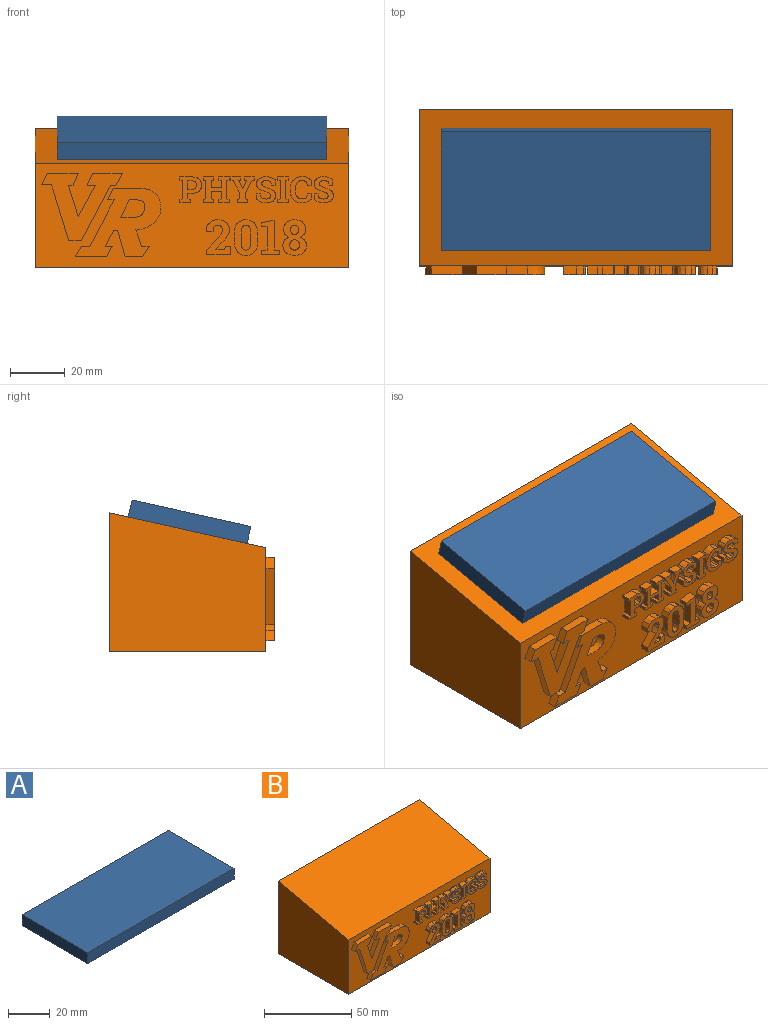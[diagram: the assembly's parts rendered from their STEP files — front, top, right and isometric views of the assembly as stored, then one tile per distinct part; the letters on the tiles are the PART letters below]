
ASSEMBLY  parts=2 mates=1
PART A: 6 faces, bbox 98.4x44.5x6.4 mm
  f0: plane 44.45x6.35mm, normal (-1,0,0), area 282.3mm2, adj f1,f3,f4,f5
  f1: plane 98.43x6.35mm, normal (0,-1,0), area 625mm2, adj f0,f2,f4,f5
  f2: plane 44.45x6.35mm, normal (1,0,0), area 282.3mm2, adj f1,f3,f4,f5
  f3: plane 98.43x6.35mm, normal (0,1,0), area 625mm2, adj f0,f2,f4,f5
  f4: plane 98.43x44.45mm, normal (0,0,1), area 4375mm2, adj f0,f1,f2,f3
  f5: plane 98.43x44.45mm, normal (0,0,-1), area 4375mm2, adj f0,f1,f2,f3
PART B: 311 faces, bbox 114.3x60.3x50.8 mm
  f0: plane 114.3x38.1mm, normal (0,-1,0), area 3082.9mm2, adj f1,f2,f4,f5,f12,f13,f14,f15
  f1: plane 57.15x50.8mm, normal (-1,0,0), area 2540.3mm2, adj f0,f3,f4,f5
  f2: plane 57.15x50.8mm, normal (1,0,0), area 2540.3mm2, adj f0,f3,f4,f5
  f3: plane 114.3x50.8mm, normal (0,1,0), area 5806.4mm2, adj f1,f2,f4,f5
  f4: plane 114.3x57.15mm, normal (0,0,-1), area 6532.2mm2, adj f0,f1,f2,f3
  f5: plane 114.3x57.15mm, normal (0,-0.22,0.98), area 6691.6mm2, adj f0,f1,f2,f3
  f6: plane 3.18x1.58mm, normal (0,0,1), area 5mm2, adj f7,f27,f28,f29
  f7: plane 3.18x3.07mm, normal (1,0,0), area 9.7mm2, adj f6,f8,f28,f29
  f8: plane 3.18x1.58mm, normal (0,0,-1), area 5mm2, adj f7,f9,f28,f29
  f9: extruded ~3.18x1.18mm, area 4.1mm2, adj f8,f10,f28,f29
  f10: extruded ~3.18x1.11mm, area 3.8mm2, adj f9,f11,f28,f29
  f11: extruded ~3.18x1.09mm, area 3.8mm2, adj f10,f27,f28,f29
  f12: extruded ~3.18x2.53mm, area 8.6mm2, adj f0,f13,f26,f28
  f13: plane 4.44x3.18mm, normal (0,0,1), area 14.1mm2, adj f0,f12,f14,f28
  f14: plane 3.18x1.13mm, normal (-1,0,0), area 3.6mm2, adj f0,f13,f15,f28
  f15: plane 3.18x0.99mm, normal (-0.19,0,-0.98), area 3.2mm2, adj f0,f14,f16,f28
  f16: plane 6.7x3.18mm, normal (-1,0,0), area 21.3mm2, adj f0,f15,f17,f28
  f17: plane 3.18x0.99mm, normal (-0.19,0,0.98), area 3.2mm2, adj f0,f16,f18,f28
  f18: plane 3.18x1.12mm, normal (-1,0,0), area 3.6mm2, adj f0,f17,f19,f28
  f19: plane 3.87x3.18mm, normal (0,0,-1), area 12.3mm2, adj f0,f18,f20,f28
  f20: plane 3.18x1.12mm, normal (1,0,0), area 3.6mm2, adj f0,f19,f21,f28
  f21: plane 3.18x1mm, normal (0.19,0,0.98), area 3.2mm2, adj f0,f20,f22,f28
  f22: plane 3.18x2.07mm, normal (1,0,0), area 6.6mm2, adj f0,f21,f23,f28
  f23: plane 3.18x1.58mm, normal (0,0,-1), area 5mm2, adj f0,f22,f24,f28
  f24: extruded ~3.18x2.53mm, area 8.6mm2, adj f0,f23,f25,f28
  f25: extruded ~3.18x2.15mm, area 7.7mm2, adj f0,f24,f26,f28
  f26: extruded ~3.18x2.16mm, area 7.7mm2, adj f0,f12,f25,f28
  f27: extruded ~3.18x1.18mm, area 4.1mm2, adj f6,f11,f28,f29
  f28: plane 9.33x7.9mm, normal (0,-1,0), area 38.4mm2, adj f6,f7,f8,f9,f10,f11,f12,f13
  f29: plane 3.16x3.07mm, normal (0,-1,0), area 8.8mm2, adj f6,f7,f8,f9,f10,f11,f27
  f30: plane 3.18x1.13mm, normal (-1,0,0), area 3.6mm2, adj f0,f31,f57,f58
  f31: plane 3.18x0.99mm, normal (-0.19,0,-0.98), area 3.2mm2, adj f0,f30,f32,f58
  f32: plane 6.7x3.18mm, normal (-1,0,0), area 21.3mm2, adj f0,f31,f33,f58
  f33: plane 3.18x0.99mm, normal (-0.19,0,0.98), area 3.2mm2, adj f0,f32,f34,f58
  f34: plane 3.18x1.12mm, normal (-1,0,0), area 3.6mm2, adj f0,f33,f35,f58
  f35: plane 3.87x3.18mm, normal (0,0,-1), area 12.3mm2, adj f0,f34,f36,f58
  f36: plane 3.18x1.12mm, normal (1,0,0), area 3.6mm2, adj f0,f35,f37,f58
  f37: plane 3.18x1mm, normal (0.19,0,0.98), area 3.2mm2, adj f0,f36,f38,f58
  f38: plane 3.18x2.56mm, normal (1,0,0), area 8.1mm2, adj f0,f37,f39,f58
  f39: plane 3.81x3.18mm, normal (0,0,-1), area 12.1mm2, adj f0,f38,f40,f58
  f40: plane 3.18x2.56mm, normal (-1,0,0), area 8.1mm2, adj f0,f39,f41,f58
  f41: plane 3.18x1mm, normal (-0.19,0,0.98), area 3.2mm2, adj f0,f40,f42,f58
  f42: plane 3.18x1.12mm, normal (-1,0,0), area 3.6mm2, adj f0,f41,f43,f58
  f43: plane 3.87x3.18mm, normal (0,0,-1), area 12.3mm2, adj f0,f42,f44,f58
  f44: plane 3.18x1.12mm, normal (1,0,0), area 3.6mm2, adj f0,f43,f45,f58
  f45: plane 3.18x1mm, normal (0.19,0,0.98), area 3.2mm2, adj f0,f44,f46,f58
  f46: plane 6.7x3.18mm, normal (1,0,0), area 21.3mm2, adj f0,f45,f47,f58
  f47: plane 3.18x1mm, normal (0.19,0,-0.98), area 3.2mm2, adj f0,f46,f48,f58
  f48: plane 3.18x1.13mm, normal (1,0,0), area 3.6mm2, adj f0,f47,f49,f58
  f49: plane 3.87x3.18mm, normal (0,0,1), area 12.3mm2, adj f0,f48,f50,f58
  f50: plane 3.18x1.13mm, normal (-1,0,0), area 3.6mm2, adj f0,f49,f51,f58
  f51: plane 3.18x1mm, normal (-0.19,0,-0.98), area 3.2mm2, adj f0,f50,f52,f58
  f52: plane 3.18x2.69mm, normal (-1,0,0), area 8.5mm2, adj f0,f51,f53,f58
  f53: plane 3.81x3.18mm, normal (0,0,1), area 12.1mm2, adj f0,f52,f54,f58
  f54: plane 3.18x2.69mm, normal (1,0,0), area 8.5mm2, adj f0,f53,f55,f58
  f55: plane 3.18x1mm, normal (0.19,0,-0.98), area 3.2mm2, adj f0,f54,f56,f58
  f56: plane 3.18x1.13mm, normal (1,0,0), area 3.6mm2, adj f0,f55,f57,f58
  f57: plane 3.87x3.18mm, normal (0,0,1), area 12.3mm2, adj f0,f30,f56,f58
  f58: plane 9.54x9.33mm, normal (0,-1,0), area 50.1mm2, adj f30,f31,f32,f33,f34,f35,f36,f37
  f59: plane 3.18x0.76mm, normal (0.14,0,-0.99), area 2.4mm2, adj f0,f60,f80,f81
  f60: plane 3.18x1.13mm, normal (1,0,0), area 3.6mm2, adj f0,f59,f61,f81
  f61: plane 3.53x3.18mm, normal (0,0,1), area 11.2mm2, adj f0,f60,f62,f81
  f62: plane 3.18x1.13mm, normal (-1,0,0), area 3.6mm2, adj f0,f61,f63,f81
  f63: plane 3.18x0.79mm, normal (-0.16,0,-0.99), area 2.5mm2, adj f0,f62,f64,f81
  f64: plane 4.7x3.18mm, normal (-0.88,0,-0.47), area 16.9mm2, adj f0,f63,f65,f81
  f65: plane 3.18x2.06mm, normal (-1,0,0), area 6.6mm2, adj f0,f64,f66,f81
  f66: plane 3.18x1mm, normal (-0.19,0,0.98), area 3.2mm2, adj f0,f65,f67,f81
  f67: plane 3.18x1.12mm, normal (-1,0,0), area 3.6mm2, adj f0,f66,f68,f81
  f68: plane 3.87x3.18mm, normal (0,0,-1), area 12.3mm2, adj f0,f67,f69,f81
  f69: plane 3.18x1.12mm, normal (1,0,0), area 3.6mm2, adj f0,f68,f70,f81
  f70: plane 3.18x1mm, normal (0.19,0,0.98), area 3.2mm2, adj f0,f69,f71,f81
  f71: plane 3.18x1.97mm, normal (1,0,0), area 6.2mm2, adj f0,f70,f72,f81
  f72: plane 4.8x3.18mm, normal (0.88,0,-0.47), area 17.2mm2, adj f0,f71,f73,f81
  f73: plane 3.18x0.8mm, normal (0.16,0,-0.99), area 2.6mm2, adj f0,f72,f74,f81
  f74: plane 3.18x1.13mm, normal (1,0,0), area 3.6mm2, adj f0,f73,f75,f81
  f75: plane 3.53x3.18mm, normal (0,0,1), area 11.2mm2, adj f0,f74,f76,f81
  f76: plane 3.18x1.13mm, normal (-1,0,0), area 3.6mm2, adj f0,f75,f77,f81
  f77: plane 3.18x0.76mm, normal (-0.14,0,-0.99), area 2.4mm2, adj f0,f76,f78,f81
  f78: plane 3.18x3.07mm, normal (-0.9,0,0.43), area 10.8mm2, adj f0,f77,f79,f81
  f79: plane 3.18x0.04mm, normal (0,0,1), area 0.1mm2, adj f0,f78,f80,f81
  f80: plane 3.18x3.07mm, normal (0.9,0,0.43), area 10.8mm2, adj f0,f59,f79,f81
  f81: plane 9.33x8.48mm, normal (0,-1,0), area 33.6mm2, adj f59,f60,f61,f62,f63,f64,f65,f66
  f82: plane 3.18x1.4mm, normal (0,0,-1), area 4.5mm2, adj f0,f83,f111,f112
  f83: plane 3.18x1.91mm, normal (1,0,0), area 6.1mm2, adj f0,f82,f84,f112
  f84: extruded ~3.18x1.49mm, area 5.5mm2, adj f0,f83,f85,f112
  f85: extruded ~3.18x1.96mm, area 6.3mm2, adj f0,f84,f86,f112
  f86: extruded ~3.18x2.42mm, area 8.2mm2, adj f0,f85,f87,f112
  f87: extruded ~3.18x1.86mm, area 6.9mm2, adj f0,f86,f88,f112
  f88: extruded ~3.18x1.81mm, area 6.6mm2, adj f0,f87,f89,f112
  f89: extruded ~3.18x2.51mm, area 8.8mm2, adj f0,f88,f90,f112
  f90: extruded ~3.18x1.34mm, area 4.7mm2, adj f0,f89,f91,f112
  f91: extruded ~3.18x0.86mm, area 3.1mm2, adj f0,f90,f92,f112
  f92: extruded ~3.18x0.84mm, area 3.1mm2, adj f0,f91,f93,f112
  f93: extruded ~3.18x1.17mm, area 3.9mm2, adj f0,f92,f94,f112
  f94: extruded ~3.18x1.08mm, area 3.5mm2, adj f0,f93,f95,f112
  f95: extruded ~3.18x0.77mm, area 2.7mm2, adj f0,f94,f96,f112
  f96: plane 3.18x1.33mm, normal (0.99,0,0.15), area 4.3mm2, adj f0,f95,f97,f112
  f97: plane 3.18x1.45mm, normal (0,0,1), area 4.6mm2, adj f0,f96,f98,f112
  f98: plane 3.18x1.95mm, normal (-1,0,0), area 6.2mm2, adj f0,f97,f99,f112
  f99: extruded ~3.18x1.49mm, area 5.7mm2, adj f0,f98,f100,f112
  f100: extruded ~3.18x2mm, area 6.5mm2, adj f0,f99,f101,f112
  f101: extruded ~3.18x2.5mm, area 8.4mm2, adj f0,f100,f102,f112
  f102: extruded ~3.18x1.89mm, area 7mm2, adj f0,f101,f103,f112
  f103: extruded ~3.18x1.85mm, area 6.6mm2, adj f0,f102,f104,f112
  f104: extruded ~3.18x2.34mm, area 8.3mm2, adj f0,f103,f105,f112
  f105: extruded ~3.18x1.52mm, area 5.2mm2, adj f0,f104,f106,f112
  f106: extruded ~3.18x0.78mm, area 3mm2, adj f0,f105,f107,f112
  f107: extruded ~3.18x0.84mm, area 3.1mm2, adj f0,f106,f108,f112
  f108: extruded ~3.18x1.19mm, area 4mm2, adj f0,f107,f109,f112
  f109: extruded ~3.18x0.99mm, area 3.2mm2, adj f0,f108,f110,f112
  f110: extruded ~3.18x0.71mm, area 2.4mm2, adj f0,f109,f111,f112
  f111: plane 3.18x1.28mm, normal (-0.98,0,-0.19), area 4.1mm2, adj f0,f82,f110,f112
  f112: plane 9.6x6.96mm, normal (0,-1,0), area 37.1mm2, adj f82,f83,f84,f85,f86,f87,f88,f89
  f113: plane 3.18x1.13mm, normal (-1,0,0), area 3.6mm2, adj f0,f114,f124,f125
  f114: plane 3.18x1mm, normal (-0.19,0,-0.98), area 3.2mm2, adj f0,f113,f115,f125
  f115: plane 6.7x3.18mm, normal (-1,0,0), area 21.3mm2, adj f0,f114,f116,f125
  f116: plane 3.18x1mm, normal (-0.19,0,0.98), area 3.2mm2, adj f0,f115,f117,f125
  f117: plane 3.18x1.12mm, normal (-1,0,0), area 3.6mm2, adj f0,f116,f118,f125
  f118: plane 3.87x3.18mm, normal (0,0,-1), area 12.3mm2, adj f0,f117,f119,f125
  f119: plane 3.18x1.12mm, normal (1,0,0), area 3.6mm2, adj f0,f118,f120,f125
  f120: plane 3.18x1mm, normal (0.19,0,0.98), area 3.2mm2, adj f0,f119,f121,f125
  f121: plane 6.7x3.18mm, normal (1,0,0), area 21.3mm2, adj f0,f120,f122,f125
  f122: plane 3.18x1mm, normal (0.19,0,-0.98), area 3.2mm2, adj f0,f121,f123,f125
  f123: plane 3.18x1.13mm, normal (1,0,0), area 3.6mm2, adj f0,f122,f124,f125
  f124: plane 3.87x3.18mm, normal (0,0,1), area 12.3mm2, adj f0,f113,f123,f125
  f125: plane 9.33x3.87mm, normal (0,-1,0), area 22.3mm2, adj f113,f114,f115,f116,f117,f118,f119,f120
  f126: plane 3.18x1.39mm, normal (0,0,-1), area 4.4mm2, adj f0,f127,f149,f150
  f127: plane 3.18x1.85mm, normal (1,0,0), area 5.9mm2, adj f0,f126,f128,f150
  f128: extruded ~3.18x1.44mm, area 5.7mm2, adj f0,f127,f129,f150
  f129: extruded ~3.18x1.96mm, area 6.4mm2, adj f0,f128,f130,f150
  f130: extruded ~3.18x3.08mm, area 11mm2, adj f0,f129,f131,f150
  f131: extruded ~3.34x3.18mm, area 11.5mm2, adj f0,f130,f132,f150
  f132: plane 3.18x0.31mm, normal (-1,0,0), area 1mm2, adj f0,f131,f133,f150
  f133: extruded ~3.34x3.18mm, area 11.5mm2, adj f0,f132,f134,f150
  f134: extruded ~3.18x3.08mm, area 10.9mm2, adj f0,f133,f135,f150
  f135: extruded ~3.18x1.96mm, area 6.4mm2, adj f0,f134,f136,f150
  f136: extruded ~3.18x1.44mm, area 5.7mm2, adj f0,f135,f137,f150
  f137: plane 3.18x1.85mm, normal (1,0,0), area 5.9mm2, adj f0,f136,f138,f150
  f138: plane 3.18x1.39mm, normal (0,0,1), area 4.4mm2, adj f0,f137,f139,f150
  f139: plane 3.18x1.24mm, normal (-0.99,0,0.15), area 4mm2, adj f0,f138,f140,f150
  f140: extruded ~3.18x0.71mm, area 2.7mm2, adj f0,f139,f141,f150
  f141: extruded ~3.18x1.01mm, area 3.3mm2, adj f0,f140,f142,f150
  f142: extruded ~3.18x1.85mm, area 6.8mm2, adj f0,f141,f143,f150
  f143: extruded ~3.18x2.32mm, area 7.8mm2, adj f0,f142,f144,f150
  f144: plane 3.18x0.33mm, normal (1,0,0), area 1mm2, adj f0,f143,f145,f150
  f145: extruded ~3.18x2.31mm, area 7.8mm2, adj f0,f144,f146,f150
  f146: extruded ~3.18x1.87mm, area 6.8mm2, adj f0,f145,f147,f150
  f147: extruded ~3.18x0.99mm, area 3.2mm2, adj f0,f146,f148,f150
  f148: extruded ~3.18x0.69mm, area 2.6mm2, adj f0,f147,f149,f150
  f149: plane 3.18x1.24mm, normal (-0.99,0,-0.15), area 4mm2, adj f0,f126,f148,f150
  f150: plane 9.61x7.67mm, normal (0,-1,0), area 33.1mm2, adj f126,f127,f128,f129,f130,f131,f132,f133
  f151: plane 3.18x1.4mm, normal (0,0,-1), area 4.5mm2, adj f0,f152,f180,f181
  f152: plane 3.18x1.91mm, normal (1,0,0), area 6.1mm2, adj f0,f151,f153,f181
  f153: extruded ~3.18x1.49mm, area 5.5mm2, adj f0,f152,f154,f181
  f154: extruded ~3.18x1.96mm, area 6.3mm2, adj f0,f153,f155,f181
  f155: extruded ~3.18x2.42mm, area 8.2mm2, adj f0,f154,f156,f181
  f156: extruded ~3.18x1.86mm, area 6.9mm2, adj f0,f155,f157,f181
  f157: extruded ~3.18x1.81mm, area 6.6mm2, adj f0,f156,f158,f181
  f158: extruded ~3.18x2.51mm, area 8.8mm2, adj f0,f157,f159,f181
  f159: extruded ~3.18x1.34mm, area 4.7mm2, adj f0,f158,f160,f181
  f160: extruded ~3.18x0.86mm, area 3.1mm2, adj f0,f159,f161,f181
  f161: extruded ~3.18x0.84mm, area 3.1mm2, adj f0,f160,f162,f181
  f162: extruded ~3.18x1.17mm, area 3.9mm2, adj f0,f161,f163,f181
  f163: extruded ~3.18x1.08mm, area 3.5mm2, adj f0,f162,f164,f181
  f164: extruded ~3.18x0.77mm, area 2.7mm2, adj f0,f163,f165,f181
  f165: plane 3.18x1.33mm, normal (0.99,0,0.15), area 4.3mm2, adj f0,f164,f166,f181
  f166: plane 3.18x1.45mm, normal (0,0,1), area 4.6mm2, adj f0,f165,f167,f181
  f167: plane 3.18x1.95mm, normal (-1,0,0), area 6.2mm2, adj f0,f166,f168,f181
  f168: extruded ~3.18x1.49mm, area 5.7mm2, adj f0,f167,f169,f181
  f169: extruded ~3.18x2mm, area 6.5mm2, adj f0,f168,f170,f181
  f170: extruded ~3.18x2.5mm, area 8.4mm2, adj f0,f169,f171,f181
  f171: extruded ~3.18x1.89mm, area 7mm2, adj f0,f170,f172,f181
  f172: extruded ~3.18x1.85mm, area 6.6mm2, adj f0,f171,f173,f181
  f173: extruded ~3.18x2.34mm, area 8.3mm2, adj f0,f172,f174,f181
  f174: extruded ~3.18x1.52mm, area 5.2mm2, adj f0,f173,f175,f181
  f175: extruded ~3.18x0.78mm, area 3mm2, adj f0,f174,f176,f181
  f176: extruded ~3.18x0.84mm, area 3.1mm2, adj f0,f175,f177,f181
  f177: extruded ~3.18x1.19mm, area 4mm2, adj f0,f176,f178,f181
  f178: extruded ~3.18x0.99mm, area 3.2mm2, adj f0,f177,f179,f181
  f179: extruded ~3.18x0.71mm, area 2.4mm2, adj f0,f178,f180,f181
  f180: plane 3.18x1.28mm, normal (-0.98,0,-0.19), area 4.1mm2, adj f0,f151,f179,f181
  f181: plane 9.6x6.96mm, normal (0,-1,0), area 37.1mm2, adj f151,f152,f153,f154,f155,f156,f157,f158
  f182: plane 3.18x1.66mm, normal (-1,0,0), area 5.3mm2, adj f0,f183,f204,f205
  f183: plane 8.62x3.18mm, normal (0,0,-1), area 27.4mm2, adj f0,f182,f184,f205
  f184: plane 3.19x3.18mm, normal (1,0,0), area 10.1mm2, adj f0,f183,f185,f205
  f185: plane 3.18x1.92mm, normal (0,0,1), area 6.1mm2, adj f0,f184,f186,f205
  f186: plane 3.18x1.25mm, normal (-1,0,0.08), area 4mm2, adj f0,f185,f187,f205
  f187: plane 3.28x3.18mm, normal (0,0,1), area 10.4mm2, adj f0,f186,f188,f205
  f188: plane 3.18x0.04mm, normal (0.94,0,0.35), area 0.2mm2, adj f0,f187,f189,f205
  f189: plane 3.18x2.45mm, normal (0.74,0,-0.68), area 10.6mm2, adj f0,f188,f190,f205
  f190: extruded ~3.18x2.54mm, area 10.4mm2, adj f0,f189,f191,f205
  f191: extruded ~3.18x2.12mm, area 7.1mm2, adj f0,f190,f192,f205
  f192: extruded ~3.18x2.71mm, area 9.6mm2, adj f0,f191,f193,f205
  f193: extruded ~3.18x3.07mm, area 10.5mm2, adj f0,f192,f194,f205
  f194: extruded ~3.18x3.15mm, area 11mm2, adj f0,f193,f195,f205
  f195: extruded ~3.18x2.89mm, area 10.1mm2, adj f0,f194,f196,f205
  f196: plane 3.18x0.05mm, normal (-0.94,0,-0.35), area 0.2mm2, adj f0,f195,f197,f205
  f197: plane 3.18x2.46mm, normal (0,0,-1), area 7.8mm2, adj f0,f196,f198,f205
  f198: extruded ~3.18x1.58mm, area 5.3mm2, adj f0,f197,f199,f205
  f199: extruded ~3.18x1.33mm, area 4.8mm2, adj f0,f198,f200,f205
  f200: extruded ~3.18x1.22mm, area 4.3mm2, adj f0,f199,f201,f205
  f201: extruded ~3.18x1.31mm, area 4.5mm2, adj f0,f200,f202,f205
  f202: extruded ~3.18x1.3mm, area 4.3mm2, adj f0,f201,f203,f205
  f203: extruded ~3.18x1.71mm, area 6.8mm2, adj f0,f202,f204,f205
  f204: plane 4.38x4.09mm, normal (-0.73,0,0.68), area 19mm2, adj f0,f182,f203,f205
  f205: plane 12.82x8.87mm, normal (0,-1,0), area 60.9mm2, adj f182,f183,f184,f185,f186,f187,f188,f189
  f206: extruded ~3.18x2.2mm, area 7.2mm2, adj f207,f225,f226,f227
  f207: plane 3.29x3.18mm, normal (-1,0,0), area 10.4mm2, adj f206,f208,f226,f227
  f208: extruded ~3.18x2.22mm, area 7.3mm2, adj f207,f209,f226,f227
  f209: extruded ~3.18x1.29mm, area 4.9mm2, adj f208,f210,f226,f227
  f210: extruded ~3.18x1.31mm, area 4.9mm2, adj f209,f211,f226,f227
  f211: extruded ~3.18x2.22mm, area 7.3mm2, adj f210,f212,f226,f227
  f212: plane 3.29x3.18mm, normal (1,0,0), area 10.4mm2, adj f211,f213,f226,f227
  f213: extruded ~3.18x2.2mm, area 7.2mm2, adj f212,f214,f226,f227
  f214: extruded ~3.18x1.3mm, area 4.9mm2, adj f213,f225,f226,f227
  f215: extruded ~3.81x3.18mm, area 12.9mm2, adj f0,f216,f224,f226
  f216: plane 3.18x2.78mm, normal (1,0,0), area 8.8mm2, adj f0,f215,f217,f226
  f217: extruded ~3.81x3.18mm, area 12.9mm2, adj f0,f216,f218,f226
  f218: extruded ~3.18x3.12mm, area 11.1mm2, adj f0,f217,f219,f226
  f219: extruded ~3.18x3.12mm, area 11.1mm2, adj f0,f218,f220,f226
  f220: extruded ~3.81x3.18mm, area 12.9mm2, adj f0,f219,f221,f226
  f221: plane 3.18x2.78mm, normal (-1,0,0), area 8.8mm2, adj f0,f220,f222,f226
  f222: extruded ~3.81x3.18mm, area 12.9mm2, adj f0,f221,f223,f226
  f223: extruded ~3.18x3.13mm, area 11.1mm2, adj f0,f222,f224,f226
  f224: extruded ~3.18x3.11mm, area 11mm2, adj f0,f215,f223,f226
  f225: extruded ~3.18x1.3mm, area 4.9mm2, adj f206,f214,f226,f227
  f226: plane 13x8.55mm, normal (0,-1,0), area 67mm2, adj f206,f207,f208,f209,f210,f211,f212,f213
  f227: plane 9.1x3.5mm, normal (0,-1,0), area 28.5mm2, adj f206,f207,f208,f209,f210,f211,f212,f213
  f228: plane 3.18x2.14mm, normal (-0.12,0,0.99), area 6.8mm2, adj f0,f229,f237,f238
  f229: plane 3.18x1.52mm, normal (-1,0,0), area 4.8mm2, adj f0,f228,f230,f238
  f230: plane 6.79x3.18mm, normal (0,0,-1), area 21.6mm2, adj f0,f229,f231,f238
  f231: plane 3.18x1.52mm, normal (1,0,0), area 4.8mm2, adj f0,f230,f232,f238
  f232: plane 3.18x2.14mm, normal (0.12,0,0.99), area 6.8mm2, adj f0,f231,f233,f238
  f233: plane 10.85x3.18mm, normal (1,0,0), area 34.5mm2, adj f0,f232,f234,f238
  f234: plane 4.68x3.18mm, normal (-0.18,0,0.98), area 15.1mm2, adj f0,f233,f235,f238
  f235: plane 3.18x1.45mm, normal (-1,0,0), area 4.6mm2, adj f0,f234,f236,f238
  f236: plane 3.18x2.16mm, normal (0,0,-1), area 6.9mm2, adj f0,f235,f237,f238
  f237: plane 8.55x3.18mm, normal (-1,0,0), area 27.2mm2, adj f0,f228,f236,f238
  f238: plane 12.63x6.82mm, normal (0,-1,0), area 41.9mm2, adj f228,f229,f230,f231,f232,f233,f234,f235
  f239: extruded ~3.18x1.23mm, area 4.2mm2, adj f240,f270,f271,f273
  f240: extruded ~3.18x1.25mm, area 4.3mm2, adj f239,f241,f271,f273
  f241: extruded ~3.18x1.08mm, area 3.9mm2, adj f240,f242,f271,f273
  f242: extruded ~3.18x1.1mm, area 3.9mm2, adj f241,f243,f271,f273
  f243: extruded ~3.18x1.25mm, area 4.3mm2, adj f242,f244,f271,f273
  f244: extruded ~3.18x1.24mm, area 4.2mm2, adj f243,f245,f271,f273
  f245: extruded ~3.18x1.08mm, area 3.9mm2, adj f244,f270,f271,f273
  f246: extruded ~3.18x1.36mm, area 4.7mm2, adj f247,f268,f271,f272
  f247: extruded ~3.18x1.36mm, area 4.7mm2, adj f246,f248,f271,f272
  f248: extruded ~3.18x1.28mm, area 4.5mm2, adj f247,f249,f271,f272
  f249: extruded ~3.18x1.29mm, area 4.5mm2, adj f248,f250,f271,f272
  f250: extruded ~3.18x1.37mm, area 4.7mm2, adj f249,f251,f271,f272
  f251: extruded ~3.18x1.36mm, area 4.7mm2, adj f250,f252,f271,f272
  f252: extruded ~3.18x1.27mm, area 4.5mm2, adj f251,f268,f271,f272
  f253: extruded ~3.18x1.68mm, area 5.6mm2, adj f0,f254,f269,f271
  f254: extruded ~3.18x2.61mm, area 9.3mm2, adj f0,f253,f255,f271
  f255: extruded ~3.18x2.92mm, area 9.9mm2, adj f0,f254,f256,f271
  f256: extruded ~3.18x2.91mm, area 9.9mm2, adj f0,f255,f257,f271
  f257: extruded ~3.18x2.61mm, area 9.3mm2, adj f0,f256,f258,f271
  f258: extruded ~3.18x1.68mm, area 5.6mm2, adj f0,f257,f259,f271
  f259: extruded ~3.18x1.38mm, area 5.7mm2, adj f0,f258,f260,f271
  f260: extruded ~3.18x1.59mm, area 6.4mm2, adj f0,f259,f261,f271
  f261: extruded ~3.18x1.81mm, area 6.1mm2, adj f0,f260,f262,f271
  f262: extruded ~3.18x2.69mm, area 9.7mm2, adj f0,f261,f263,f271
  f263: extruded ~3.18x3.12mm, area 10.6mm2, adj f0,f262,f264,f271
  f264: extruded ~3.18x3.1mm, area 10.5mm2, adj f0,f263,f265,f271
  f265: extruded ~3.18x2.69mm, area 9.7mm2, adj f0,f264,f266,f271
  f266: extruded ~3.18x1.8mm, area 6.1mm2, adj f0,f265,f267,f271
  f267: extruded ~3.18x1.59mm, area 6.4mm2, adj f0,f266,f269,f271
  f268: extruded ~3.18x1.29mm, area 4.5mm2, adj f246,f252,f271,f272
  f269: extruded ~3.18x1.38mm, area 5.7mm2, adj f0,f253,f267,f271
  f270: extruded ~3.18x1.09mm, area 3.9mm2, adj f239,f245,f271,f273
  f271: plane 13x8.61mm, normal (0,-1,0), area 71.7mm2, adj f239,f240,f241,f242,f243,f244,f245,f246
  f272: plane 3.74x3.55mm, normal (0,-1,0), area 10.7mm2, adj f246,f247,f248,f249,f250,f251,f252,f268
  f273: plane 3.41x2.96mm, normal (0,-1,0), area 8.2mm2, adj f239,f240,f241,f242,f243,f244,f245,f270
  f274: plane 4.43x3.18mm, normal (0.92,0,-0.39), area 15.3mm2, adj f0,f275,f288,f289
  f275: plane 11.23x3.18mm, normal (0,0,1), area 35.6mm2, adj f0,f274,f276,f289
  f276: plane 4.34x3.18mm, normal (-0.89,0,0.45), area 15.4mm2, adj f0,f275,f277,f289
  f277: plane 3.68x3.18mm, normal (0,0,-1), area 11.7mm2, adj f0,f276,f278,f289
  f278: plane 20.38x6.23mm, normal (-0.96,0,-0.29), area 67.7mm2, adj f0,f277,f279,f289
  f279: plane 4.62x3.18mm, normal (0,0,-1), area 14.7mm2, adj f0,f278,f280,f289
  f280: plane 20.29x10.66mm, normal (0.89,0,-0.47), area 72.8mm2, adj f0,f279,f281,f289
  f281: plane 3.18x1.98mm, normal (0,0,-1), area 6.3mm2, adj f0,f280,f282,f289
  f282: plane 4.43x3.18mm, normal (0.89,0,-0.45), area 15.8mm2, adj f0,f281,f283,f289
  f283: plane 10.76x3.18mm, normal (0,0,1), area 34.2mm2, adj f0,f282,f284,f289
  f284: plane 4.43x3.18mm, normal (-0.91,0,0.42), area 15.5mm2, adj f0,f283,f285,f289
  f285: plane 3.18x3.02mm, normal (0,0,-1), area 9.6mm2, adj f0,f284,f286,f289
  f286: plane 11.51x6.23mm, normal (-0.88,0,0.48), area 41.6mm2, adj f0,f285,f287,f289
  f287: plane 11.51x3.59mm, normal (0.95,0,0.3), area 38.3mm2, adj f0,f286,f288,f289
  f288: plane 3.18x1.7mm, normal (0,0,-1), area 5.4mm2, adj f0,f274,f287,f289
  f289: plane 29.44x24.72mm, normal (0,-1,0), area 305.8mm2, adj f274,f275,f276,f277,f278,f279,f280,f281
  f290: plane 10.87x3.18mm, normal (0,0,1), area 34.5mm2, adj f0,f291,f308,f309
  f291: plane 4.15x3.18mm, normal (-0.9,0,0.44), area 14.7mm2, adj f0,f290,f292,f309
  f292: plane 3.18x2.36mm, normal (0,0,-1), area 7.5mm2, adj f0,f291,f293,f309
  f293: plane 16.89x8.87mm, normal (-0.89,0,0.46), area 60.6mm2, adj f0,f292,f294,f309
  f294: plane 3.18x3.11mm, normal (0,0,1), area 9.9mm2, adj f0,f293,f295,f309
  f295: plane 3.8x3.18mm, normal (-0.87,0,0.5), area 14mm2, adj f0,f294,f296,f309
  f296: plane 11.44x3.18mm, normal (0,0,-1), area 36.3mm2, adj f0,f295,f297,f309
  f297: plane 3.7x3.18mm, normal (0.88,0,-0.47), area 13.3mm2, adj f0,f296,f298,f309
  f298: plane 3.18x2.57mm, normal (0,0,1), area 8.2mm2, adj f0,f297,f299,f309
  f299: plane 5.99x3.18mm, normal (0.89,0,-0.46), area 21.5mm2, adj f0,f298,f300,f309
  f300: plane 3.18x1.46mm, normal (0,0,-1), area 4.7mm2, adj f0,f299,f301,f309
  f301: plane 9.69x3.18mm, normal (-0.96,0,-0.27), area 32mm2, adj f0,f300,f302,f309
  f302: plane 6.39x3.18mm, normal (0,0,-1), area 20.3mm2, adj f0,f301,f303,f309
  f303: plane 3.7x3.18mm, normal (0.84,0,-0.54), area 14mm2, adj f0,f302,f304,f309
  f304: plane 3.18x2.74mm, normal (0,0,1), area 8.7mm2, adj f0,f303,f305,f309
  f305: plane 6.05x3.18mm, normal (0.94,0,0.33), area 20.3mm2, adj f0,f304,f308,f309
  f306: plane 6.27x3.18mm, normal (0.89,0,-0.45), area 22.3mm2, adj f307,f309,f310
  f307: extruded ~8.85x6.46mm, area 58mm2, adj f306,f309,f310
  f308: extruded ~15.09x9.07mm, area 76.7mm2, adj f0,f290,f305,f309
  f309: plane 31.25x24.84mm, normal (0,-1,0), area 374.3mm2, adj f290,f291,f292,f293,f294,f295,f296,f297
  f310: plane 8.87x6.5mm, normal (0,-1,0), area 42.4mm2, adj f306,f307
PLACE A rot(axis=(1,0,0),12.5deg) t=(-24.11,9.11,36.32)mm
PLACE B t=(-32.05,2.23,-3.31)mm
MATE planar A.f5 <-> B.f5  axis (0,0.22,-0.98) through (25.1,30.81,41.14)mm
